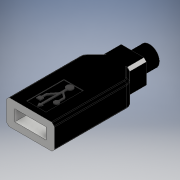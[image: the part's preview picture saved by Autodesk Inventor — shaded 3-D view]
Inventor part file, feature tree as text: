
AUTODESK INVENTOR PART (.ipt)
format: ipt  version: 2018 (Build 220112000, 112)  size: 336,896 bytes
history: native  units: mm
features: sketch x8, extrude x6, fillet x3, chamfer x2, plane x1
ambient origin geometry x8: Origin, YZ Plane, XZ Plane, XY Plane, X Axis, Y Axis, Z Axis, Center Point
bodies: Solid1 (feature_tree)
feature tree (20):
  extrude  "Extrusion1"  Depth=30.0mm
  chamfer  "Chamfer1"  Distance=10.0mm
  fillet  "Fillet1"  Radius=0.5mm
  fillet  "Fillet2"  Radius=3.0mm
  fillet  "Fillet3"  Radius=3.0mm
  extrude  "Extrusion2"  Depth=14.9mm
  extrude  "Extrusion7"  Depth=0.3mm TaperAngle=0.0deg
  plane  "Work Plane1"
  extrude  "Extrusion14"  Depth=12.5mm
  sketch  "Sketch18"  dims[d14=7.75mm d15=14.9mm]
  sketch  "Sketch19"  dims[d16=2.3mm d17=0.3mm d18=0.0mm]
  extrude  "Extrusion15"  Depth=6.75mm TaperAngle=0.0deg
  chamfer  "Chamfer2"  Distance=2.26mm
  extrude  "Extrusion16"  Depth=11.04mm
  sketch  "Sketch1"  dims[d2=19.05mm d3=30.0mm]
  sketch  "Sketch2"  dims[d4=11.04mm]
  sketch  "Sketch8"  dims[d5=4.0mm d6=10.0mm d7=0.0mm]
  sketch  "Sketch17"  dims[d8=1.0mm d9=2.0mm d10=45.0deg d11=0.5mm d12=3.0mm d13=3.0mm]
  sketch  "Sketch20"  dims[d71=0.3mm d72=0.0mm d101=12.5mm]
  sketch  "Sketch21"  dims[d102=4.52mm d106=20.0mm d107=0.0mm d108=2.26mm d109=11.04mm d110=6.6mm d111=0.0mm d112=1.0mm d113=2.0mm d114=45.0deg d115=7.9mm d116=6.75mm d117=0.0mm]
